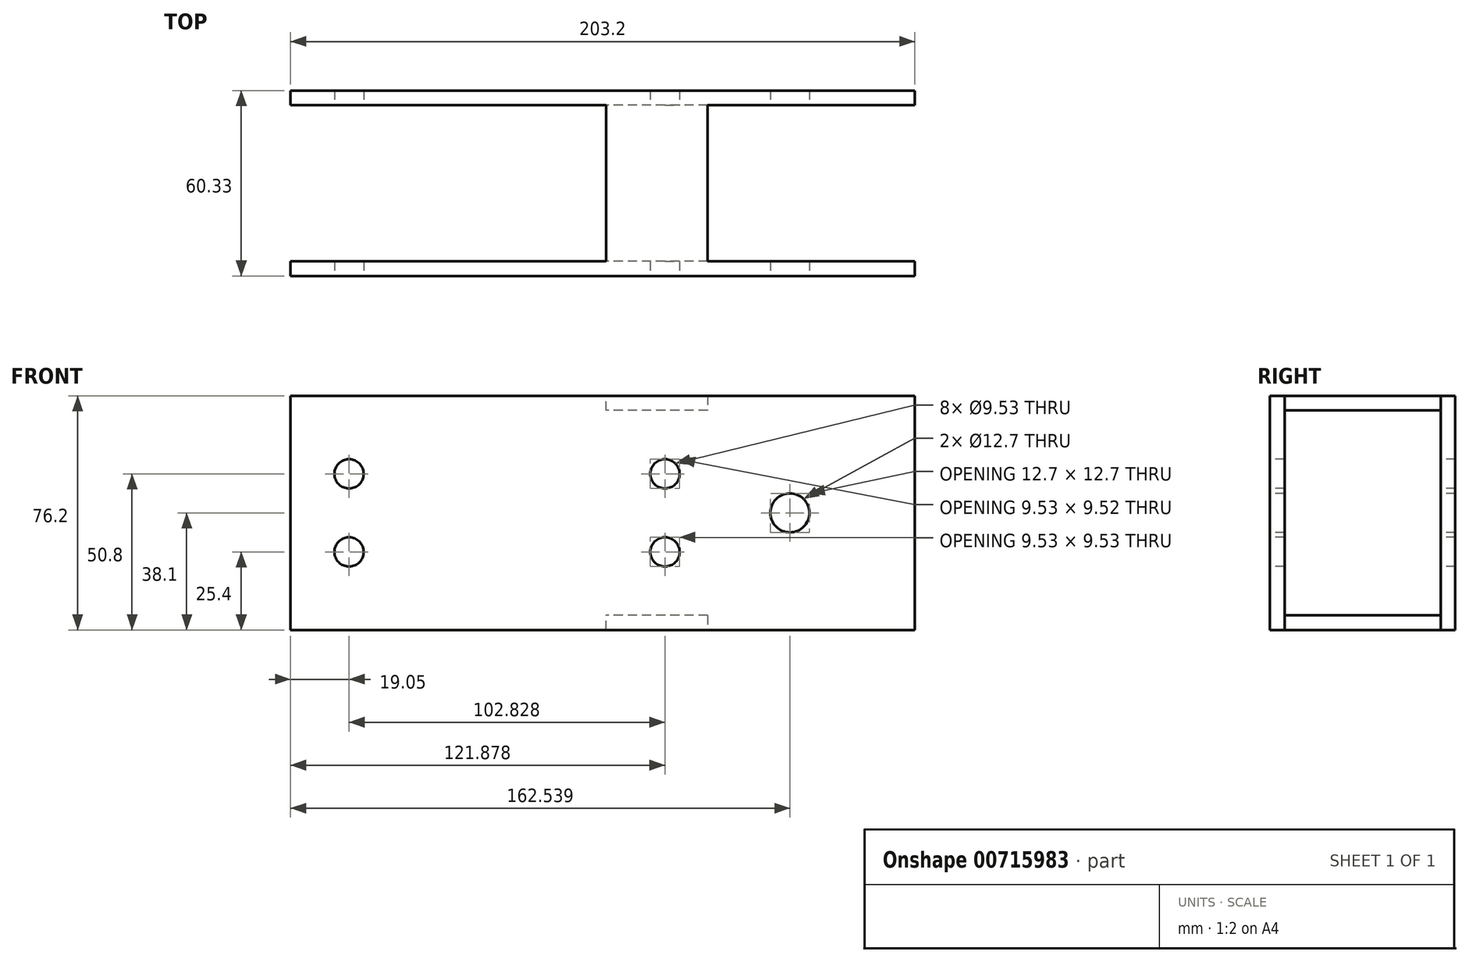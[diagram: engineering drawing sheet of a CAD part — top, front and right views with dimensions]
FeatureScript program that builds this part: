
annotation { "Feature Type Name" : "Feature", "Feature Type Description" : "" }
export const myFeature = defineFeature(function(context is Context, id is Id, definition is map)
    precondition{}
    {
        {
            var Q0;
            Q0=qCreatedBy(makeId("Front.planeOp"),FACE);
            var sketch = newSketch(context, id + "F0", { "sketchPlane" : qUnion([Q0])});
            skLineSegment(sketch, "E0", {"start": v(0, 0) * mm, "end": v(203.2, 0) * mm, "construction": true});
            skLineSegment(sketch, "E1", {"start": v(0, 0) * mm, "end": v(0, 76.2) * mm, "construction": true});
            skLineSegment(sketch, "E2", {"start": v(0, 76.2) * mm, "end": v(203.2, 76.2) * mm, "construction": true});
            skLineSegment(sketch, "E3", {"start": v(203.2, 0) * mm, "end": v(203.2, 76.2) * mm, "construction": true});
            skLineSegment(sketch, "E4", {"start": v(0, 76.2) * mm, "end": v(19.05, 76.2) * mm, "construction": true});
            skLineSegment(sketch, "E5", {"start": v(19.05, 76.2) * mm, "end": v(19.05, 0) * mm, "construction": true});
            skLineSegment(sketch, "E6", {"start": v(0, 76.2) * mm, "end": v(0, 50.8) * mm, "construction": true});
            skLineSegment(sketch, "E7", {"start": v(0, 0) * mm, "end": v(0, 25.4) * mm, "construction": true});
            skLineSegment(sketch, "E8", {"start": v(0, 50.8) * mm, "end": v(203.2, 50.8) * mm, "construction": true});
            skLineSegment(sketch, "E9", {"start": v(0, 25.4) * mm, "end": v(203.2, 25.4) * mm, "construction": true});
            skCircle(sketch, "E10", {"center": v(19.05, 50.8) * mm, "radius": 4.76 * mm});
            skCircle(sketch, "E11", {"center": v(19.05, 25.4) * mm, "radius": 4.76 * mm});
            skLineSegment(sketch, "E12", {"start": v(30.66, 76.2) * mm, "end": v(30.66, 0) * mm, "construction": true});
            skLineSegment(sketch, "E13", {"start": v(30.66, 76.2) * mm, "end": v(106.86, 76.2) * mm, "construction": true});
            skLineSegment(sketch, "E14", {"start": v(106.86, 76.2) * mm, "end": v(106.86, 0) * mm, "construction": true});
            skLineSegment(sketch, "E15", {"start": v(121.88, 76.2) * mm, "end": v(121.88, 0) * mm, "construction": true});
            skLineSegment(sketch, "E16", {"start": v(203.2, 38.1) * mm, "end": v(121.88, 38.1) * mm, "construction": true});
            skLineSegment(sketch, "E17", {"start": v(0, 76.2) * mm, "end": v(203.2, 76.2) * mm});
            skLineSegment(sketch, "E18", {"start": v(203.2, 76.2) * mm, "end": v(203.2, 0) * mm});
            skLineSegment(sketch, "E19", {"start": v(203.2, 0) * mm, "end": v(0, 0) * mm});
            skLineSegment(sketch, "E20", {"start": v(0, 0) * mm, "end": v(0, 76.2) * mm});
            skCircle(sketch, "E21", {"center": v(121.88, 50.8) * mm, "radius": 4.76 * mm});
            skCircle(sketch, "E22", {"center": v(121.88, 25.4) * mm, "radius": 4.76 * mm});
            skCircle(sketch, "E23", {"center": v(162.54, 38.1) * mm, "radius": 6.35 * mm});
            skSolve(sketch);
        }
        {
            var Q0;
            Q0 = qSketchRegion(id + "F0", true);
            var Q1;
            Q1=makeQuery(id+"F0.imprint","IMPRINT",FACE,{"disambiguationData":[TD([[makeQuery(id+"F0.imprint","IMPRINT",EDGE,{"derivedFrom":sQuery(id+"F0.wireOp",EDGE,"E10")}),-1.0]])]});
            extrude(context, id + "F1", {"entities" : qUnion([Q0, Q1]), "oppositeDirection" : true, "depth" : 60.32 * mm, "offsetDistance" : 25.4 * mm});
        }
        {
            var Q0;
            Q0=makeQuery(id+"F1.opExtrude","SWEPT_FACE",FACE,{"disambiguationData":[OSD([sQuery(id+"F0.wireOp",EDGE,"E17")])]});
            cPlane(context, id + "F2", {"entities" : qUnion([Q0]), "cplaneType" : CPlaneType.OFFSET, "offset" : 0 * mm, "width" : 152.4 * mm, "height" : 152.4 * mm});
        }
        {
            var Q0;
            Q0=qCreatedBy(id+"F2.planeOp",FACE);
            var sketch = newSketch(context, id + "F3", { "sketchPlane" : qUnion([Q0])});
            skLineSegment(sketch, "E24", {"start": v(102.76, 60.33) * mm, "end": v(0, 60.33) * mm});
            skLineSegment(sketch, "E25", {"start": v(0, 60.33) * mm, "end": v(0, 0) * mm});
            skLineSegment(sketch, "E26", {"start": v(0, 0) * mm, "end": v(102.76, 0) * mm});
            skLineSegment(sketch, "E27.0", {"start": v(102.76, 55.56) * mm, "end": v(0, 55.56) * mm});
            skLineSegment(sketch, "E28.0", {"start": v(0, 4.76) * mm, "end": v(102.76, 4.76) * mm});
            skLineSegment(sketch, "E29", {"start": v(102.76, 55.56) * mm, "end": v(102.76, 4.76) * mm});
            skSolve(sketch);
        }
        {
            var Q0;
            {var subQ0=sQuery(id+"F3.wireOp",EDGE,"E27.0");Q0=makeQuery(id+"F3.imprint","IMPRINT",FACE,{"disambiguationData":[TD([[makeQuery(id+"F3.imprint","IMPRINT",EDGE,{"derivedFrom":subQ0}),1.0]])]});}
            extrude(context, id + "F4", {"entities" : qUnion([Q0]), "operationType" : NewBodyOperationType.REMOVE, "oppositeDirection" : true, "depth" : 85.72 * mm, "offsetDistance" : 25.4 * mm});
        }
        {
            var Q0;
            Q0=qCreatedBy(makeId("Right.planeOp"),FACE);
            var sketch = newSketch(context, id + "F5", { "sketchPlane" : qUnion([Q0])});
            skLineSegment(sketch, "E30.0", {"start": v(4.76, 71.44) * mm, "end": v(4.76, 4.76) * mm});
            skLineSegment(sketch, "E31.0", {"start": v(55.56, 71.44) * mm, "end": v(55.56, 4.76) * mm});
            skLineSegment(sketch, "E32.0", {"start": v(55.56, 71.44) * mm, "end": v(4.76, 71.44) * mm});
            skLineSegment(sketch, "E33.0", {"start": v(55.56, 4.76) * mm, "end": v(4.76, 4.76) * mm});
            skSolve(sketch);
        }
        {
            var Q0;
            Q0 = qSketchRegion(id + "F5", true);
            extrude(context, id + "F6", {"entities" : qUnion([Q0]), "operationType" : NewBodyOperationType.REMOVE, "depth" : 203.2 * mm, "offsetDistance" : 25.4 * mm});
        }
        {
            var Q0;
            Q0=qCreatedBy(makeId("Top.planeOp"),FACE);
            var sketch = newSketch(context, id + "F7", { "sketchPlane" : qUnion([Q0])});
            skLineSegment(sketch, "E34", {"start": v(135.8, 55.56) * mm, "end": v(135.8, 4.76) * mm});
            skLineSegment(sketch, "E35.0", {"start": v(135.8, 55.56) * mm, "end": v(203.2, 55.56) * mm});
            skLineSegment(sketch, "E36.0", {"start": v(135.8, 4.76) * mm, "end": v(203.2, 4.76) * mm});
            skPoint(sketch, "E37.orphan", {"position": v(135.8, 0) * mm});
            skLineSegment(sketch, "E38", {"start": v(203.2, 4.76) * mm, "end": v(203.2, 55.56) * mm});
            skSolve(sketch);
        }
        {
            var Q0;
            Q0 = qSketchRegion(id + "F7", true);
            extrude(context, id + "F8", {"entities" : qUnion([Q0]), "operationType" : NewBodyOperationType.REMOVE, "depth" : 76.2 * mm, "offsetDistance" : 25.4 * mm});
        }
    });
